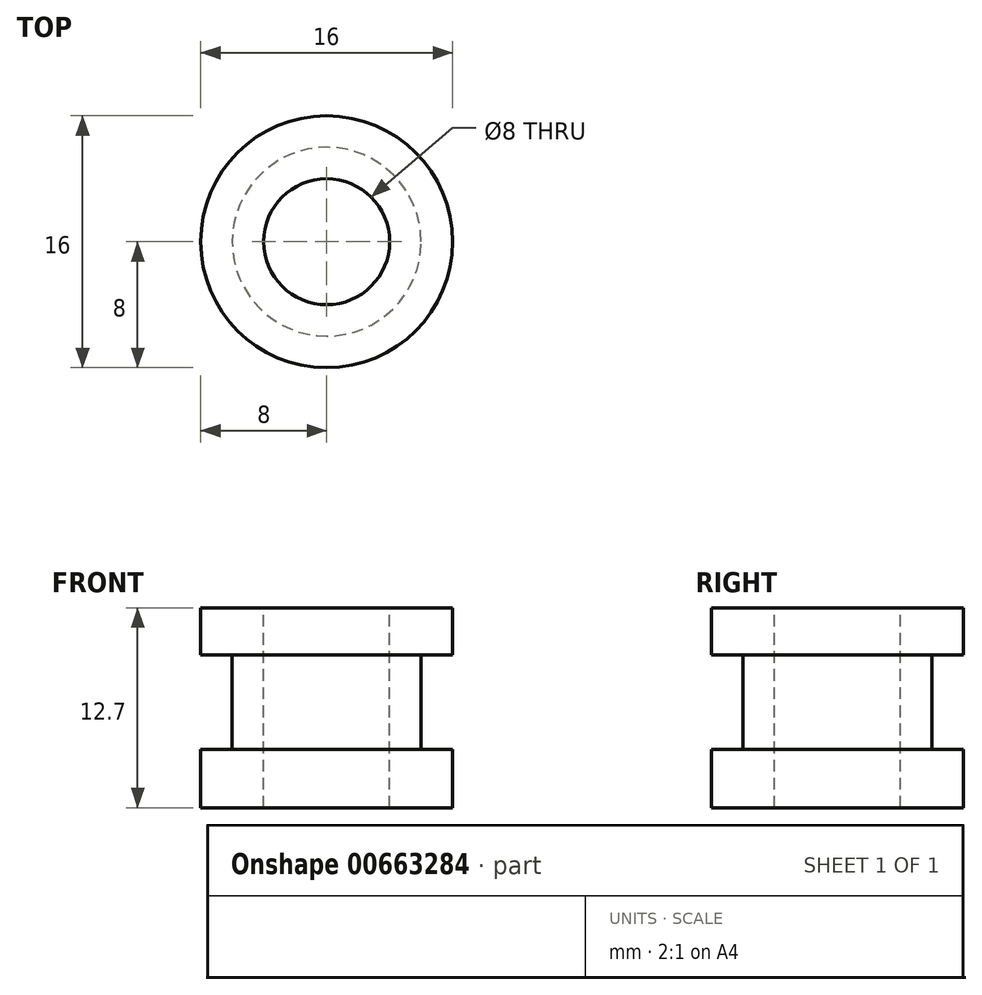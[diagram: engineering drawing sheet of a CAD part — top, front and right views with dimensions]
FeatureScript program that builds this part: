
annotation { "Feature Type Name" : "Feature", "Feature Type Description" : "" }
export const myFeature = defineFeature(function(context is Context, id is Id, definition is map)
    precondition{}
    {
        {
            var Q0;
            Q0=qCreatedBy(makeId("Top.planeOp"),FACE);
            var sketch = newSketch(context, id + "F0", { "sketchPlane" : qUnion([Q0])});
            skCircle(sketch, "E0", {"center": v(0, 0) * mm, "radius": 8 * mm});
            skSolve(sketch);
        }
        {
            var Q0;
            Q0 = qSketchRegion(id + "F0", true);
            extrude(context, id + "F1", {"entities" : qUnion([Q0]), "depth" : 3.7 * mm, "offsetDistance" : 25 * mm});
        }
        {
            var Q0;
            Q0=makeQuery(id+"F1.opExtrude","CAP_FACE",FACE,{"disambiguationData":[OSD([sQuery(id+"F0.wireOp",EDGE,"E0")])],"isStart":false});
            var sketch = newSketch(context, id + "F2", { "sketchPlane" : qUnion([Q0])});
            skCircle(sketch, "E1", {"center": v(0, 0) * mm, "radius": 6 * mm});
            skSolve(sketch);
        }
        {
            var Q0;
            Q0 = qSketchRegion(id + "F2", true);
            extrude(context, id + "F3", {"entities" : qUnion([Q0]), "operationType" : NewBodyOperationType.ADD, "depth" : 6 * mm, "offsetDistance" : 25 * mm});
        }
        {
            var Q0;
            Q0=makeQuery(id+"F3.opExtrude","CAP_FACE",FACE,{"disambiguationData":[OSD([sQuery(id+"F2.wireOp",EDGE,"E1")])],"isStart":false});
            var sketch = newSketch(context, id + "F4", { "sketchPlane" : qUnion([Q0])});
            skCircle(sketch, "E2", {"center": v(0, 0) * mm, "radius": 8 * mm});
            skSolve(sketch);
        }
        {
            var Q0;
            Q0 = qSketchRegion(id + "F4", true);
            extrude(context, id + "F5", {"entities" : qUnion([Q0]), "operationType" : NewBodyOperationType.ADD, "depth" : 3 * mm, "offsetDistance" : 25 * mm});
        }
        {
            var Q0;
            Q0=makeQuery(id+"F5.opExtrude","CAP_FACE",FACE,{"disambiguationData":[OSD([sQuery(id+"F4.wireOp",EDGE,"E2")])],"isStart":false});
            var sketch = newSketch(context, id + "F6", { "sketchPlane" : qUnion([Q0])});
            skCircle(sketch, "E3", {"center": v(0, 0) * mm, "radius": 4 * mm});
            skSolve(sketch);
        }
        {
            var Q0;
            Q0 = qSketchRegion(id + "F6", true);
            extrude(context, id + "F7", {"entities" : qUnion([Q0]), "operationType" : NewBodyOperationType.REMOVE, "oppositeDirection" : true, "depth" : 25 * mm, "offsetDistance" : 25 * mm});
        }
    });
